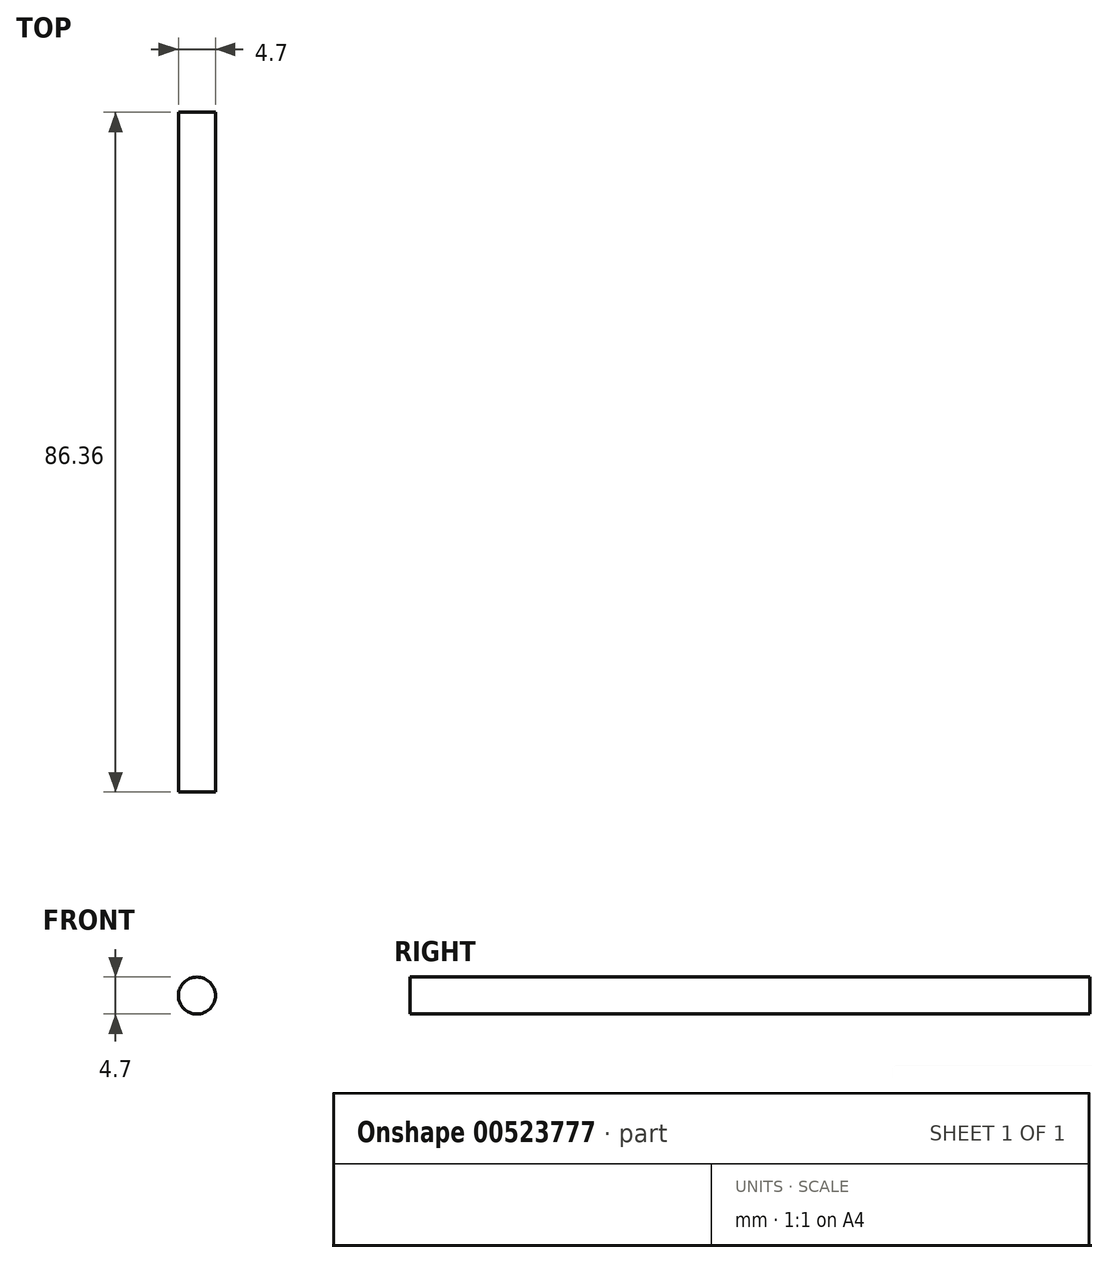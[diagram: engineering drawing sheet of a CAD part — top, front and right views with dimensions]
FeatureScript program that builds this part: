
annotation { "Feature Type Name" : "Feature", "Feature Type Description" : "" }
export const myFeature = defineFeature(function(context is Context, id is Id, definition is map)
    precondition{}
    {
        {
            var Q0;
            Q0=qCreatedBy(makeId("Front.planeOp"),FACE);
            var sketch = newSketch(context, id + "F0", { "sketchPlane" : qUnion([Q0])});
            skCircle(sketch, "E0", {"center": v(0, -1.4) * mm, "radius": 2.35 * mm});
            skSolve(sketch);
        }
        {
            var Q0;
            Q0=makeQuery(id+"F0.imprint","IMPRINT",FACE,{"disambiguationData":[TD([[makeQuery(id+"F0.imprint","IMPRINT",EDGE,{"derivedFrom":sQuery(id+"F0.wireOp",EDGE,"E0")}),1.0]])]});
            extrude(context, id + "F1", {"entities" : qUnion([Q0]), "depth" : 86.36 * mm, "offsetDistance" : 25.4 * mm});
        }
    });
